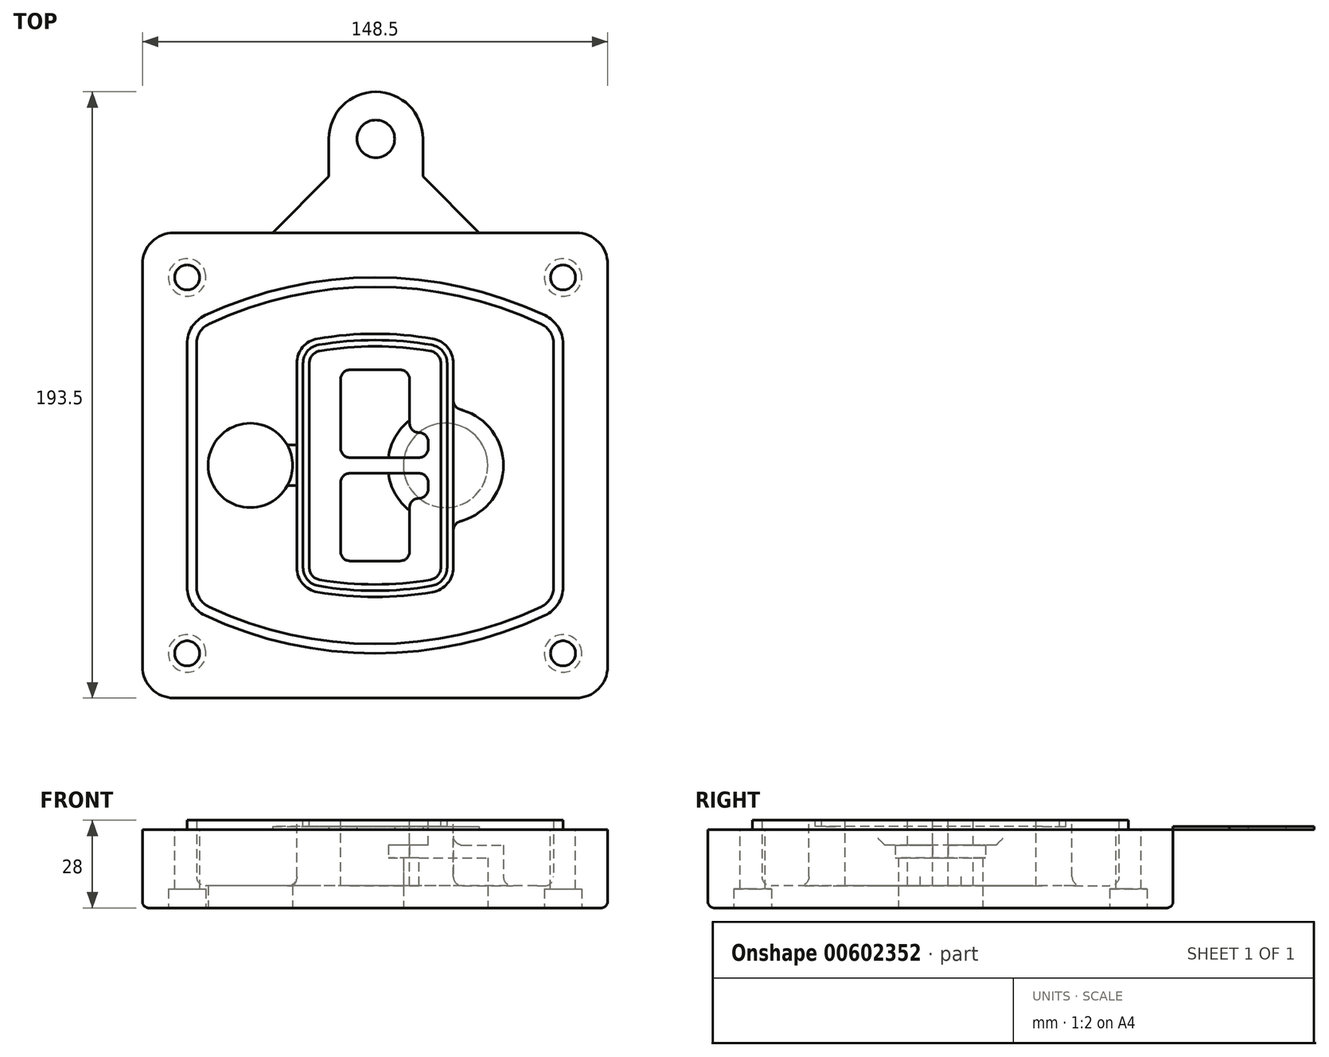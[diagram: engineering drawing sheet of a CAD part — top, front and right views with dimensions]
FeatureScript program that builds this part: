
annotation { "Feature Type Name" : "Feature", "Feature Type Description" : "" }
export const myFeature = defineFeature(function(context is Context, id is Id, definition is map)
    precondition{}
    {
        {
            var Q0;
            Q0=qCreatedBy(makeId("Top.planeOp"),FACE);
            var sketch = newSketch(context, id + "F0", { "sketchPlane" : qUnion([Q0])});
            skPoint(sketch, "E0.rect.middle", {"position": v(0, 0) * mm});
            skLineSegment(sketch, "E1.bottom", {"start": v(-64.25, -74.25) * mm, "end": v(64.25, -74.25) * mm});
            skLineSegment(sketch, "E1.top", {"start": v(-64.25, 74.25) * mm, "end": v(64.25, 74.25) * mm});
            skLineSegment(sketch, "E1.left", {"start": v(-74.25, -64.25) * mm, "end": v(-74.25, 64.25) * mm});
            skLineSegment(sketch, "E1.right", {"start": v(74.25, -64.25) * mm, "end": v(74.25, 64.25) * mm});
            skLineSegment(sketch, "E2", {"start": v(-74.25, 74.25) * mm, "end": v(74.25, -74.25) * mm, "construction": true});
            skLineSegment(sketch, "E3", {"start": v(74.25, 74.25) * mm, "end": v(-74.25, -74.25) * mm, "construction": true});
            skCircle(sketch, "E4", {"center": v(-60, 60) * mm, "radius": 4 * mm});
            skCircle(sketch, "E5", {"center": v(60, 60) * mm, "radius": 4 * mm});
            skCircle(sketch, "E6", {"center": v(60, -60) * mm, "radius": 4 * mm});
            skCircle(sketch, "E7", {"center": v(-60, -60) * mm, "radius": 4 * mm});
            skLineSegment(sketch, "E8", {"start": v(-60, 60) * mm, "end": v(60, 60) * mm, "construction": true});
            skLineSegment(sketch, "E9", {"start": v(60, 60) * mm, "end": v(60, -60) * mm, "construction": true});
            skLineSegment(sketch, "E10", {"start": v(60, -60) * mm, "end": v(-60, -60) * mm, "construction": true});
            skLineSegment(sketch, "E11", {"start": v(-60, -60) * mm, "end": v(-60, 60) * mm, "construction": true});
            skLineSegment(sketch, "E12", {"start": v(-60, 38.83) * mm, "end": v(-60, -38.83) * mm});
            skLineSegment(sketch, "E13", {"start": v(60, 38.83) * mm, "end": v(60, -38.83) * mm});
            skArc(sketch, "E14", {"start": v(54.26, 47.88) * mm, "mid": v(0, 60) * mm, "end": v(-54.26, 47.88) * mm});
            skArc(sketch, "E15", {"start": v(-54.26, -47.88) * mm, "mid": v(0, -60) * mm, "end": v(54.26, -47.88) * mm});
            skLineSegment(sketch, "E16", {"start": v(-60, 0) * mm, "end": v(60, 0) * mm, "construction": true});
            skPoint(sketch, "E17.visualSharp", {"position": v(-60, -45) * mm});
            skArc(sketch, "E17.filletArc", {"start": v(-60, -38.83) * mm, "mid": v(-58.44, -44.2) * mm, "end": v(-54.26, -47.88) * mm});
            skPoint(sketch, "E18.visualSharp", {"position": v(-60, 45) * mm});
            skArc(sketch, "E18.filletArc", {"start": v(-54.26, 47.88) * mm, "mid": v(-58.44, 44.2) * mm, "end": v(-60, 38.83) * mm});
            skPoint(sketch, "E19.visualSharp", {"position": v(60, 45) * mm});
            skArc(sketch, "E19.filletArc", {"start": v(60, 38.83) * mm, "mid": v(58.44, 44.2) * mm, "end": v(54.26, 47.88) * mm});
            skPoint(sketch, "E20.visualSharp", {"position": v(60, -45) * mm});
            skArc(sketch, "E20.filletArc", {"start": v(54.26, -47.88) * mm, "mid": v(58.44, -44.2) * mm, "end": v(60, -38.83) * mm});
            skPoint(sketch, "E21.visualSharp", {"position": v(-74.25, 74.25) * mm});
            skArc(sketch, "E21.filletArc", {"start": v(-64.25, 74.25) * mm, "mid": v(-71.32, 71.32) * mm, "end": v(-74.25, 64.25) * mm});
            skPoint(sketch, "E22.visualSharp", {"position": v(74.25, 74.25) * mm});
            skArc(sketch, "E22.filletArc", {"start": v(74.25, 64.25) * mm, "mid": v(71.32, 71.32) * mm, "end": v(64.25, 74.25) * mm});
            skPoint(sketch, "E23.visualSharp", {"position": v(74.25, -74.25) * mm});
            skArc(sketch, "E23.filletArc", {"start": v(64.25, -74.25) * mm, "mid": v(71.32, -71.32) * mm, "end": v(74.25, -64.25) * mm});
            skPoint(sketch, "E24.visualSharp", {"position": v(-74.25, -74.25) * mm});
            skArc(sketch, "E24.filletArc", {"start": v(-74.25, -64.25) * mm, "mid": v(-71.32, -71.32) * mm, "end": v(-64.25, -74.25) * mm});
            skArc(sketch, "E25.0", {"start": v(57, 38.83) * mm, "mid": v(55.9, 42.58) * mm, "end": v(52.98, 45.17) * mm});
            skLineSegment(sketch, "E25.1", {"start": v(57, 38.83) * mm, "end": v(57, -38.83) * mm});
            skArc(sketch, "E25.2", {"start": v(52.98, -45.17) * mm, "mid": v(55.9, -42.58) * mm, "end": v(57, -38.83) * mm});
            skArc(sketch, "E25.3", {"start": v(-52.98, -45.17) * mm, "mid": v(0, -57) * mm, "end": v(52.98, -45.17) * mm});
            skArc(sketch, "E25.4", {"start": v(-57, -38.83) * mm, "mid": v(-55.9, -42.58) * mm, "end": v(-52.98, -45.17) * mm});
            skArc(sketch, "E25.5", {"start": v(52.98, 45.17) * mm, "mid": v(0, 57) * mm, "end": v(-52.98, 45.17) * mm});
            skLineSegment(sketch, "E25.6", {"start": v(-57, 38.83) * mm, "end": v(-57, -38.83) * mm});
            skArc(sketch, "E25.7", {"start": v(-52.98, 45.17) * mm, "mid": v(-55.9, 42.58) * mm, "end": v(-57, 38.83) * mm});
            skArc(sketch, "E26.0", {"start": v(-55.96, 51.5) * mm, "mid": v(-61.82, 46.33) * mm, "end": v(-64, 38.83) * mm});
            skArc(sketch, "E26.1", {"start": v(55.96, 51.5) * mm, "mid": v(0, 64) * mm, "end": v(-55.96, 51.5) * mm});
            skArc(sketch, "E26.2", {"start": v(64, 38.83) * mm, "mid": v(61.82, 46.33) * mm, "end": v(55.96, 51.5) * mm});
            skLineSegment(sketch, "E26.3", {"start": v(64, 38.83) * mm, "end": v(64, -38.83) * mm});
            skArc(sketch, "E26.4", {"start": v(55.96, -51.5) * mm, "mid": v(61.82, -46.33) * mm, "end": v(64, -38.83) * mm});
            skLineSegment(sketch, "E26.5", {"start": v(-64, 38.83) * mm, "end": v(-64, -38.83) * mm});
            skArc(sketch, "E26.6", {"start": v(-55.96, -51.5) * mm, "mid": v(0, -64) * mm, "end": v(55.96, -51.5) * mm});
            skArc(sketch, "E26.7", {"start": v(-64, -38.83) * mm, "mid": v(-61.82, -46.33) * mm, "end": v(-55.96, -51.5) * mm});
            skSolve(sketch);
        }
        {
            var Q0;
            Q0=makeQuery(id+"F0.imprint","IMPRINT",FACE,{"disambiguationData":[TD([[makeQuery(id+"F0.imprint","IMPRINT",EDGE,{"derivedFrom":sQuery(id+"F0.wireOp",EDGE,"E1.bottom")}),1.0]])]});
            var Q1;
            Q1=makeQuery(id+"F0.imprint","IMPRINT",FACE,{"disambiguationData":[TD([[makeQuery(id+"F0.imprint","IMPRINT",EDGE,{"derivedFrom":sQuery(id+"F0.wireOp",EDGE,"E12")}),1.0]])]});
            var Q2;
            Q2=makeQuery(id+"F0.imprint","IMPRINT",FACE,{"disambiguationData":[TD([[makeQuery(id+"F0.imprint","IMPRINT",EDGE,{"derivedFrom":sQuery(id+"F0.wireOp",EDGE,"E25.0")}),1.0]])]});
            var Q3;
            Q3=makeQuery(id+"F0.imprint","IMPRINT",FACE,{"disambiguationData":[TD([[makeQuery(id+"F0.imprint","IMPRINT",EDGE,{"derivedFrom":sQuery(id+"F0.wireOp",EDGE,"E12")}),-1.0]])]});
            extrude(context, id + "F1", {"entities" : qUnion([Q0, Q1, Q2, Q3]), "oppositeDirection" : true, "depth" : 25 * mm});
        }
        {
            var Q0;
            Q0=makeQuery(id+"F0.imprint","IMPRINT",FACE,{"disambiguationData":[TD([[makeQuery(id+"F0.imprint","IMPRINT",EDGE,{"derivedFrom":sQuery(id+"F0.wireOp",EDGE,"E12")}),1.0]])]});
            extrude(context, id + "F2", {"entities" : qUnion([Q0]), "operationType" : NewBodyOperationType.ADD, "depth" : 3 * mm});
        }
        {
            var Q0;
            Q0=makeQuery(id+"F0.imprint","IMPRINT",FACE,{"disambiguationData":[TD([[makeQuery(id+"F0.imprint","IMPRINT",EDGE,{"derivedFrom":sQuery(id+"F0.wireOp",EDGE,"E25.0")}),1.0]])]});
            extrude(context, id + "F3", {"entities" : qUnion([Q0]), "operationType" : NewBodyOperationType.REMOVE, "oppositeDirection" : true, "depth" : 18 * mm});
        }
        {
            var Q0;
            Q0=makeQuery(id+"F2.opExtrude","CAP_FACE",FACE,{"disambiguationData":[OSD([sQuery(id+"F0.wireOp",EDGE,"E12"),sQuery(id+"F0.wireOp",EDGE,"E13"),sQuery(id+"F0.wireOp",EDGE,"E14"),sQuery(id+"F0.wireOp",EDGE,"E15"),sQuery(id+"F0.wireOp",EDGE,"E17.filletArc"),sQuery(id+"F0.wireOp",EDGE,"E18.filletArc"),sQuery(id+"F0.wireOp",EDGE,"E19.filletArc"),sQuery(id+"F0.wireOp",EDGE,"E20.filletArc"),sQuery(id+"F0.wireOp",EDGE,"E25.0"),sQuery(id+"F0.wireOp",EDGE,"E25.1"),sQuery(id+"F0.wireOp",EDGE,"E25.2"),sQuery(id+"F0.wireOp",EDGE,"E25.3"),sQuery(id+"F0.wireOp",EDGE,"E25.4"),sQuery(id+"F0.wireOp",EDGE,"E25.5"),sQuery(id+"F0.wireOp",EDGE,"E25.6"),sQuery(id+"F0.wireOp",EDGE,"E25.7")])],"isStart":false});
            var sketch = newSketch(context, id + "F4", { "sketchPlane" : qUnion([Q0])});
            skArc(sketch, "E27.0", {"start": v(-18.34, -40.45) * mm, "mid": v(0, -42) * mm, "end": v(18.34, -40.45) * mm});
            skArc(sketch, "E28.0", {"start": v(18.34, 40.45) * mm, "mid": v(0, 42) * mm, "end": v(-18.34, 40.45) * mm});
            skLineSegment(sketch, "E29", {"start": v(-25, 32.57) * mm, "end": v(-25, -32.57) * mm});
            skLineSegment(sketch, "E30", {"start": v(25, 32.57) * mm, "end": v(25, -32.57) * mm});
            skLineSegment(sketch, "E31", {"start": v(-25, 39.1) * mm, "end": v(25, 39.1) * mm, "construction": true});
            skLineSegment(sketch, "E32", {"start": v(-25, -39.1) * mm, "end": v(25, -39.1) * mm, "construction": true});
            skPoint(sketch, "E33.visualSharp", {"position": v(-25, 39.1) * mm});
            skArc(sketch, "E33.filletArc", {"start": v(-18.34, 40.45) * mm, "mid": v(-23.11, 37.73) * mm, "end": v(-25, 32.57) * mm});
            skPoint(sketch, "E34.visualSharp", {"position": v(25, 39.1) * mm});
            skArc(sketch, "E34.filletArc", {"start": v(25, 32.57) * mm, "mid": v(23.11, 37.73) * mm, "end": v(18.34, 40.45) * mm});
            skPoint(sketch, "E35.visualSharp", {"position": v(25, -39.1) * mm});
            skArc(sketch, "E35.filletArc", {"start": v(18.34, -40.45) * mm, "mid": v(23.11, -37.73) * mm, "end": v(25, -32.57) * mm});
            skPoint(sketch, "E36.visualSharp", {"position": v(-25, -39.1) * mm});
            skArc(sketch, "E36.filletArc", {"start": v(-25, -32.57) * mm, "mid": v(-23.11, -37.73) * mm, "end": v(-18.34, -40.45) * mm});
            skArc(sketch, "E37.0", {"start": v(52.98, 45.17) * mm, "mid": v(0, 57) * mm, "end": v(-52.98, 45.17) * mm});
            skArc(sketch, "E37.1", {"start": v(-52.98, 45.17) * mm, "mid": v(-55.9, 42.58) * mm, "end": v(-57, 38.83) * mm});
            skLineSegment(sketch, "E37.2", {"start": v(-57, 38.83) * mm, "end": v(-57, -38.83) * mm});
            skArc(sketch, "E37.3", {"start": v(-57, -38.83) * mm, "mid": v(-55.9, -42.58) * mm, "end": v(-52.98, -45.17) * mm});
            skArc(sketch, "E37.4", {"start": v(-52.98, -45.17) * mm, "mid": v(0, -57) * mm, "end": v(52.98, -45.17) * mm});
            skArc(sketch, "E37.5", {"start": v(52.98, -45.17) * mm, "mid": v(55.9, -42.58) * mm, "end": v(57, -38.83) * mm});
            skLineSegment(sketch, "E37.6", {"start": v(57, 38.83) * mm, "end": v(57, -38.83) * mm});
            skArc(sketch, "E37.7", {"start": v(57, 38.83) * mm, "mid": v(55.9, 42.58) * mm, "end": v(52.98, 45.17) * mm});
            skLineSegment(sketch, "E38.0", {"start": v(23, 32.57) * mm, "end": v(23, -32.57) * mm});
            skArc(sketch, "E38.1", {"start": v(18, -38.48) * mm, "mid": v(21.58, -36.44) * mm, "end": v(23, -32.57) * mm});
            skArc(sketch, "E38.2", {"start": v(-18, -38.48) * mm, "mid": v(0, -40) * mm, "end": v(18, -38.48) * mm});
            skArc(sketch, "E38.3", {"start": v(-23, -32.57) * mm, "mid": v(-21.58, -36.44) * mm, "end": v(-18, -38.48) * mm});
            skLineSegment(sketch, "E38.4", {"start": v(-23, 32.57) * mm, "end": v(-23, -32.57) * mm});
            skArc(sketch, "E38.5", {"start": v(23, 32.57) * mm, "mid": v(21.58, 36.44) * mm, "end": v(18, 38.48) * mm});
            skArc(sketch, "E38.6", {"start": v(-18, 38.48) * mm, "mid": v(-21.58, 36.44) * mm, "end": v(-23, 32.57) * mm});
            skArc(sketch, "E38.7", {"start": v(18, 38.48) * mm, "mid": v(0, 40) * mm, "end": v(-18, 38.48) * mm});
            skArc(sketch, "E39.0", {"start": v(21, 32.57) * mm, "mid": v(20.06, 35.15) * mm, "end": v(17.67, 36.5) * mm});
            skLineSegment(sketch, "E39.1", {"start": v(21, 32.57) * mm, "end": v(21, -32.57) * mm});
            skArc(sketch, "E39.2", {"start": v(17.67, -36.5) * mm, "mid": v(20.06, -35.15) * mm, "end": v(21, -32.57) * mm});
            skArc(sketch, "E39.3", {"start": v(-17.67, -36.5) * mm, "mid": v(0, -38) * mm, "end": v(17.67, -36.5) * mm});
            skArc(sketch, "E39.4", {"start": v(-21, -32.57) * mm, "mid": v(-20.06, -35.15) * mm, "end": v(-17.67, -36.5) * mm});
            skArc(sketch, "E39.5", {"start": v(17.67, 36.5) * mm, "mid": v(0, 38) * mm, "end": v(-17.67, 36.5) * mm});
            skLineSegment(sketch, "E39.6", {"start": v(-21, 32.57) * mm, "end": v(-21, -32.57) * mm});
            skArc(sketch, "E39.7", {"start": v(-17.67, 36.5) * mm, "mid": v(-20.06, 35.15) * mm, "end": v(-21, 32.57) * mm});
            skLineSegment(sketch, "E40", {"start": v(-25, 0) * mm, "end": v(25, 0) * mm, "construction": true});
            skLineSegment(sketch, "E41", {"start": v(-11, 5.5) * mm, "end": v(-11, 27.5) * mm});
            skLineSegment(sketch, "E42", {"start": v(-8, 30.5) * mm, "end": v(8, 30.5) * mm});
            skLineSegment(sketch, "E43", {"start": v(11, 27.5) * mm, "end": v(11, 13.5) * mm});
            skLineSegment(sketch, "E44", {"start": v(14, 10.5) * mm, "end": v(14, 10.5) * mm});
            skLineSegment(sketch, "E45", {"start": v(17, 7.5) * mm, "end": v(17, 5.5) * mm});
            skLineSegment(sketch, "E46", {"start": v(14, 2.5) * mm, "end": v(-8, 2.5) * mm});
            skPoint(sketch, "E47.visualSharp", {"position": v(-11, 30.5) * mm});
            skArc(sketch, "E47.filletArc", {"start": v(-8, 30.5) * mm, "mid": v(-10.12, 29.62) * mm, "end": v(-11, 27.5) * mm});
            skPoint(sketch, "E48.visualSharp", {"position": v(11, 30.5) * mm});
            skArc(sketch, "E48.filletArc", {"start": v(11, 27.5) * mm, "mid": v(10.12, 29.62) * mm, "end": v(8, 30.5) * mm});
            skPoint(sketch, "E49.visualSharp", {"position": v(11, 10.5) * mm});
            skArc(sketch, "E49.filletArc", {"start": v(11, 13.5) * mm, "mid": v(11.88, 11.38) * mm, "end": v(14, 10.5) * mm});
            skPoint(sketch, "E50.visualSharp", {"position": v(17, 10.5) * mm});
            skArc(sketch, "E50.filletArc", {"start": v(17, 7.5) * mm, "mid": v(16.12, 9.62) * mm, "end": v(14, 10.5) * mm});
            skPoint(sketch, "E51.visualSharp", {"position": v(17, 2.5) * mm});
            skArc(sketch, "E51.filletArc", {"start": v(14, 2.5) * mm, "mid": v(16.12, 3.38) * mm, "end": v(17, 5.5) * mm});
            skPoint(sketch, "E52.visualSharp", {"position": v(-11, 2.5) * mm});
            skArc(sketch, "E52.filletArc", {"start": v(-11, 5.5) * mm, "mid": v(-10.12, 3.38) * mm, "end": v(-8, 2.5) * mm});
            skLineSegment(sketch, "E53.0.MirrorCS", {"start": v(14, -2.5) * mm, "end": v(-8, -2.5) * mm});
            skArc(sketch, "E54.0.MirrorCS", {"start": v(-11, -5.5) * mm, "mid": v(-10.12, -3.38) * mm, "end": v(-8, -2.5) * mm});
            skLineSegment(sketch, "E55.0.MirrorCS", {"start": v(-11, -5.5) * mm, "end": v(-11, -27.5) * mm});
            skArc(sketch, "E56.0.MirrorCS", {"start": v(-8, -30.5) * mm, "mid": v(-10.12, -29.62) * mm, "end": v(-11, -27.5) * mm});
            skLineSegment(sketch, "E57.0.MirrorCS", {"start": v(-8, -30.5) * mm, "end": v(8, -30.5) * mm});
            skArc(sketch, "E58.0.MirrorCS", {"start": v(11, -27.5) * mm, "mid": v(10.12, -29.62) * mm, "end": v(8, -30.5) * mm});
            skLineSegment(sketch, "E59.0.MirrorCS", {"start": v(11, -27.5) * mm, "end": v(11, -13.5) * mm});
            skArc(sketch, "E60.0.MirrorCS", {"start": v(11, -13.5) * mm, "mid": v(11.88, -11.38) * mm, "end": v(14, -10.5) * mm});
            skArc(sketch, "E61.0.MirrorCS", {"start": v(17, -7.5) * mm, "mid": v(16.12, -9.62) * mm, "end": v(14, -10.5) * mm});
            skLineSegment(sketch, "E62.0.MirrorCS", {"start": v(17, -7.5) * mm, "end": v(17, -5.5) * mm});
            skArc(sketch, "E63.0.MirrorCS", {"start": v(14, -2.5) * mm, "mid": v(16.12, -3.38) * mm, "end": v(17, -5.5) * mm});
            skSolve(sketch);
        }
        {
            var Q0;
            Q0=makeQuery(id+"F4.imprint","IMPRINT",FACE,{"disambiguationData":[TD([[makeQuery(id+"F4.imprint","IMPRINT",EDGE,{"derivedFrom":sQuery(id+"F4.wireOp",EDGE,"E27.0")}),1.0]])]});
            var Q1;
            Q1=makeQuery(id+"F4.imprint","IMPRINT",FACE,{"disambiguationData":[TD([[makeQuery(id+"F4.imprint","IMPRINT",EDGE,{"derivedFrom":sQuery(id+"F4.wireOp",EDGE,"E38.0")}),-1.0]])]});
            var Q2;
            Q2=makeQuery(id+"F4.imprint","IMPRINT",FACE,{"disambiguationData":[TD([[makeQuery(id+"F4.imprint","IMPRINT",EDGE,{"derivedFrom":sQuery(id+"F4.wireOp",EDGE,"E39.0")}),1.0]])]});
            extrude(context, id + "F5", {"entities" : qUnion([Q0, Q1, Q2]), "operationType" : NewBodyOperationType.ADD, "endBound" : BoundingType.UP_TO_NEXT, "oppositeDirection" : true, "depth" : 25 * mm});
        }
        {
            var Q0;
            Q0=makeQuery(id+"F4.imprint","IMPRINT",FACE,{"disambiguationData":[TD([[makeQuery(id+"F4.imprint","IMPRINT",EDGE,{"derivedFrom":sQuery(id+"F4.wireOp",EDGE,"E38.0")}),-1.0]])]});
            extrude(context, id + "F6", {"entities" : qUnion([Q0]), "operationType" : NewBodyOperationType.REMOVE, "oppositeDirection" : true, "depth" : 2 * mm});
        }
        {
            var Q0;
            Q0=makeQuery(id+"F1.opExtrude","CAP_FACE",FACE,{"disambiguationData":[OSD([sQuery(id+"F0.wireOp",EDGE,"E1.bottom"),sQuery(id+"F0.wireOp",EDGE,"E1.top"),sQuery(id+"F0.wireOp",EDGE,"E1.left"),sQuery(id+"F0.wireOp",EDGE,"E1.right"),sQuery(id+"F0.wireOp",EDGE,"E4"),sQuery(id+"F0.wireOp",EDGE,"E5"),sQuery(id+"F0.wireOp",EDGE,"E6"),sQuery(id+"F0.wireOp",EDGE,"E7"),sQuery(id+"F0.wireOp",EDGE,"E21.filletArc"),sQuery(id+"F0.wireOp",EDGE,"E22.filletArc"),sQuery(id+"F0.wireOp",EDGE,"E23.filletArc"),sQuery(id+"F0.wireOp",EDGE,"E24.filletArc")])],"isStart":false});
            var sketch = newSketch(context, id + "F7", { "sketchPlane" : qUnion([Q0])});
            skCircle(sketch, "E64", {"center": v(22.5, 0) * mm, "radius": 13.47 * mm});
            skCircle(sketch, "E65", {"center": v(-39.81, 0) * mm, "radius": 13.47 * mm});
            skLineSegment(sketch, "E66", {"start": v(74.25, 0) * mm, "end": v(-74.25, 0) * mm});
            skCircle(sketch, "E67", {"center": v(22.5, 0) * mm, "radius": 18.47 * mm});
            skCircle(sketch, "E68", {"center": v(60, -60) * mm, "radius": 6 * mm});
            skCircle(sketch, "E69", {"center": v(-60, -60) * mm, "radius": 6 * mm});
            skCircle(sketch, "E70", {"center": v(-60, 60) * mm, "radius": 6 * mm});
            skCircle(sketch, "E71", {"center": v(60, 60) * mm, "radius": 6 * mm});
            skSolve(sketch);
        }
        {
            var Q0;
            {var subQ1=sQuery(id+"F7.wireOp",EDGE,"E66");var subQ4=sQuery(id+"F7.wireOp",EDGE,"E64");var subQ6=makeQuery(id+"F7.imprint","INTERSECT",VERTEX,{"disambiguationData":[OD(0.0)],"derivedFrom":[subQ4,subQ1]});Q0=makeQuery(id+"F7.imprint","IMPRINT",FACE,{"disambiguationData":[TD([[makeQuery(id+"F7.imprint","IMPRINT",EDGE,{"disambiguationData":[TD([[subQ6,-1.0]])],"derivedFrom":subQ4}),-1.0]])]});}
            var Q1;
            {var subQ0=sQuery(id+"F7.wireOp",EDGE,"E66");var subQ1=sQuery(id+"F7.wireOp",EDGE,"E64");var subQ3=makeQuery(id+"F7.imprint","INTERSECT",VERTEX,{"disambiguationData":[OD(0.0)],"derivedFrom":[subQ1,subQ0]});Q1=makeQuery(id+"F7.imprint","IMPRINT",FACE,{"disambiguationData":[TD([[makeQuery(id+"F7.imprint","IMPRINT",EDGE,{"disambiguationData":[TD([[subQ3,-1.0]])],"derivedFrom":subQ1}),1.0]])]});}
            var Q2;
            {var subQ0=sQuery(id+"F7.wireOp",EDGE,"E66");var subQ1=sQuery(id+"F7.wireOp",EDGE,"E64");var subQ3=makeQuery(id+"F7.imprint","INTERSECT",VERTEX,{"disambiguationData":[OD(0.0)],"derivedFrom":[subQ1,subQ0]});Q2=makeQuery(id+"F7.imprint","IMPRINT",FACE,{"disambiguationData":[TD([[makeQuery(id+"F7.imprint","IMPRINT",EDGE,{"disambiguationData":[TD([[subQ3,1.0]])],"derivedFrom":subQ1}),1.0]])]});}
            var Q3;
            {var subQ1=sQuery(id+"F7.wireOp",EDGE,"E66");var subQ4=sQuery(id+"F7.wireOp",EDGE,"E64");var subQ6=makeQuery(id+"F7.imprint","INTERSECT",VERTEX,{"disambiguationData":[OD(0.0)],"derivedFrom":[subQ4,subQ1]});Q3=makeQuery(id+"F7.imprint","IMPRINT",FACE,{"disambiguationData":[TD([[makeQuery(id+"F7.imprint","IMPRINT",EDGE,{"disambiguationData":[TD([[subQ6,1.0]])],"derivedFrom":subQ4}),-1.0]])]});}
            extrude(context, id + "F8", {"entities" : qUnion([Q0, Q1, Q2, Q3]), "operationType" : NewBodyOperationType.ADD, "oppositeDirection" : true, "depth" : 20 * mm});
        }
        {
            var Q0;
            {var subQ0=sQuery(id+"F7.wireOp",EDGE,"E66");var subQ1=sQuery(id+"F7.wireOp",EDGE,"E64");var subQ3=makeQuery(id+"F7.imprint","INTERSECT",VERTEX,{"disambiguationData":[OD(0.0)],"derivedFrom":[subQ1,subQ0]});Q0=makeQuery(id+"F7.imprint","IMPRINT",FACE,{"disambiguationData":[TD([[makeQuery(id+"F7.imprint","IMPRINT",EDGE,{"disambiguationData":[TD([[subQ3,-1.0]])],"derivedFrom":subQ1}),1.0]])]});}
            var Q1;
            {var subQ0=sQuery(id+"F7.wireOp",EDGE,"E66");var subQ1=sQuery(id+"F7.wireOp",EDGE,"E64");var subQ3=makeQuery(id+"F7.imprint","INTERSECT",VERTEX,{"disambiguationData":[OD(0.0)],"derivedFrom":[subQ1,subQ0]});Q1=makeQuery(id+"F7.imprint","IMPRINT",FACE,{"disambiguationData":[TD([[makeQuery(id+"F7.imprint","IMPRINT",EDGE,{"disambiguationData":[TD([[subQ3,1.0]])],"derivedFrom":subQ1}),1.0]])]});}
            extrude(context, id + "F9", {"entities" : qUnion([Q0, Q1]), "operationType" : NewBodyOperationType.REMOVE, "oppositeDirection" : true, "depth" : 16 * mm});
        }
        {
            var Q0;
            {var subQ0=sQuery(id+"F7.wireOp",EDGE,"E66");var subQ1=sQuery(id+"F7.wireOp",EDGE,"E65");var subQ3=makeQuery(id+"F7.imprint","INTERSECT",VERTEX,{"disambiguationData":[OD(0.0)],"derivedFrom":[subQ1,subQ0]});Q0=makeQuery(id+"F7.imprint","IMPRINT",FACE,{"disambiguationData":[TD([[makeQuery(id+"F7.imprint","IMPRINT",EDGE,{"disambiguationData":[TD([[subQ3,-1.0]])],"derivedFrom":subQ1}),1.0]])]});}
            var Q1;
            {var subQ0=sQuery(id+"F7.wireOp",EDGE,"E66");var subQ1=sQuery(id+"F7.wireOp",EDGE,"E65");var subQ3=makeQuery(id+"F7.imprint","INTERSECT",VERTEX,{"disambiguationData":[OD(0.0)],"derivedFrom":[subQ1,subQ0]});Q1=makeQuery(id+"F7.imprint","IMPRINT",FACE,{"disambiguationData":[TD([[makeQuery(id+"F7.imprint","IMPRINT",EDGE,{"disambiguationData":[TD([[subQ3,1.0]])],"derivedFrom":subQ1}),1.0]])]});}
            extrude(context, id + "F10", {"entities" : qUnion([Q0, Q1]), "operationType" : NewBodyOperationType.REMOVE, "oppositeDirection" : true, "depth" : 25 * mm});
        }
        {
            var Q0;
            Q0=makeQuery(id+"F7.imprint","IMPRINT",FACE,{"disambiguationData":[TD([[makeQuery(id+"F7.imprint","IMPRINT",EDGE,{"derivedFrom":sQuery(id+"F7.wireOp",EDGE,"E68")}),1.0]])]});
            var Q1;
            Q1=makeQuery(id+"F7.imprint","IMPRINT",FACE,{"disambiguationData":[TD([[makeQuery(id+"F7.imprint","IMPRINT",EDGE,{"derivedFrom":makeQuery(id+"F1.opExtrude","CAP_EDGE",EDGE,{"disambiguationData":[OSD([sQuery(id+"F0.wireOp",EDGE,"E5")])],"isStart":false})}),-1.0]])]});
            var Q2;
            Q2=makeQuery(id+"F7.imprint","IMPRINT",FACE,{"disambiguationData":[TD([[makeQuery(id+"F7.imprint","IMPRINT",EDGE,{"derivedFrom":sQuery(id+"F7.wireOp",EDGE,"E69")}),1.0]])]});
            var Q3;
            Q3=makeQuery(id+"F7.imprint","IMPRINT",FACE,{"disambiguationData":[TD([[makeQuery(id+"F7.imprint","IMPRINT",EDGE,{"derivedFrom":makeQuery(id+"F1.opExtrude","CAP_EDGE",EDGE,{"disambiguationData":[OSD([sQuery(id+"F0.wireOp",EDGE,"E4")])],"isStart":false})}),-1.0]])]});
            var Q4;
            Q4=makeQuery(id+"F7.imprint","IMPRINT",FACE,{"disambiguationData":[TD([[makeQuery(id+"F7.imprint","IMPRINT",EDGE,{"derivedFrom":sQuery(id+"F7.wireOp",EDGE,"E70")}),1.0]])]});
            var Q5;
            Q5=makeQuery(id+"F7.imprint","IMPRINT",FACE,{"disambiguationData":[TD([[makeQuery(id+"F7.imprint","IMPRINT",EDGE,{"derivedFrom":makeQuery(id+"F1.opExtrude","CAP_EDGE",EDGE,{"disambiguationData":[OSD([sQuery(id+"F0.wireOp",EDGE,"E7")])],"isStart":false})}),-1.0]])]});
            var Q6;
            Q6=makeQuery(id+"F7.imprint","IMPRINT",FACE,{"disambiguationData":[TD([[makeQuery(id+"F7.imprint","IMPRINT",EDGE,{"derivedFrom":sQuery(id+"F7.wireOp",EDGE,"E71")}),1.0]])]});
            var Q7;
            Q7=makeQuery(id+"F7.imprint","IMPRINT",FACE,{"disambiguationData":[TD([[makeQuery(id+"F7.imprint","IMPRINT",EDGE,{"derivedFrom":makeQuery(id+"F1.opExtrude","CAP_EDGE",EDGE,{"disambiguationData":[OSD([sQuery(id+"F0.wireOp",EDGE,"E6")])],"isStart":false})}),-1.0]])]});
            extrude(context, id + "F11", {"entities" : qUnion([Q0, Q1, Q2, Q3, Q4, Q5, Q6, Q7]), "operationType" : NewBodyOperationType.REMOVE, "oppositeDirection" : true, "depth" : 6 * mm});
        }
        {
            var Q0;
            Q0=makeQuery(id+"F9.boolean.opBoolean","COPY",FACE,{"derivedFrom":makeQuery(id+"F9.opExtrude","CAP_FACE",FACE,{"disambiguationData":[OSD([sQuery(id+"F7.wireOp",EDGE,"E64")])],"isStart":false})});
            var sketch = newSketch(context, id + "F12", { "sketchPlane" : qUnion([Q0])});
            skArc(sketch, "E72.0", {"start": v(11, 14.45) * mm, "mid": v(6.45, 9.13) * mm, "end": v(4.2, 2.5) * mm});
            skArc(sketch, "E72.1", {"start": v(4.2, -2.5) * mm, "mid": v(6.45, -9.13) * mm, "end": v(11, -14.45) * mm});
            skLineSegment(sketch, "E73", {"start": v(4.2, -2.5) * mm, "end": v(14, -2.5) * mm});
            skLineSegment(sketch, "E74.0", {"start": v(14, 2.5) * mm, "end": v(4.2, 2.5) * mm});
            skArc(sketch, "E74.1", {"start": v(14, 2.5) * mm, "mid": v(16.12, 3.38) * mm, "end": v(17, 5.5) * mm});
            skLineSegment(sketch, "E74.2", {"start": v(17, 7.5) * mm, "end": v(17, 5.5) * mm});
            skArc(sketch, "E74.3", {"start": v(17, 7.5) * mm, "mid": v(16.12, 9.62) * mm, "end": v(14, 10.5) * mm});
            skArc(sketch, "E74.4", {"start": v(11, 13.5) * mm, "mid": v(11.88, 11.38) * mm, "end": v(14, 10.5) * mm});
            skLineSegment(sketch, "E74.5", {"start": v(11, 14.45) * mm, "end": v(11, 13.5) * mm});
            skLineSegment(sketch, "E74.7", {"start": v(14, -2.5) * mm, "end": v(4.2, -2.5) * mm});
            skArc(sketch, "E74.8", {"start": v(14, -2.5) * mm, "mid": v(16.12, -3.38) * mm, "end": v(17, -5.5) * mm});
            skLineSegment(sketch, "E74.9", {"start": v(17, -7.5) * mm, "end": v(17, -5.5) * mm});
            skArc(sketch, "E74.10", {"start": v(17, -7.5) * mm, "mid": v(16.12, -9.62) * mm, "end": v(14, -10.5) * mm});
            skArc(sketch, "E74.11", {"start": v(11, -13.5) * mm, "mid": v(11.88, -11.38) * mm, "end": v(14, -10.5) * mm});
            skLineSegment(sketch, "E74.12", {"start": v(11, -14.45) * mm, "end": v(11, -13.5) * mm});
            skPoint(sketch, "E75.orphan", {"position": v(11, -27.5) * mm});
            skPoint(sketch, "E76.orphan", {"position": v(-8, -2.5) * mm});
            skPoint(sketch, "E77.orphan", {"position": v(-8, 2.5) * mm});
            skPoint(sketch, "E78.orphan", {"position": v(11, 27.5) * mm});
            skSolve(sketch);
        }
        {
            var Q0;
            {var subQ7=sQuery(id+"F12.wireOp",EDGE,"E72.0");var subQ14=sQuery(id+"F12.wireOp",EDGE,"E72.1");var subQ16=sQuery(id+"F12.wireOp",EDGE,"E74.1");var subQ18=sQuery(id+"F12.wireOp",EDGE,"E74.8");Q0=qUnion([makeQuery(id+"F12.imprint","IMPRINT",FACE,{"disambiguationData":[TD([[makeQuery(id+"F12.imprint","IMPRINT",EDGE,{"derivedFrom":subQ7}),1.0]])]}),makeQuery(id+"F12.imprint","IMPRINT",FACE,{"disambiguationData":[TD([[makeQuery(id+"F12.imprint","IMPRINT",EDGE,{"derivedFrom":subQ14}),1.0]])]}),makeQuery(id+"F12.imprint","IMPRINT",FACE,{"disambiguationData":[TD([[makeQuery(id+"F12.imprint","IMPRINT",EDGE,{"derivedFrom":subQ16}),1.0]])]}),makeQuery(id+"F12.imprint","IMPRINT",FACE,{"disambiguationData":[TD([[makeQuery(id+"F12.imprint","IMPRINT",EDGE,{"derivedFrom":subQ18}),-1.0]])]})]);}
            var Q1;
            Q1=makeQuery(id+"F5.boolean.opBoolean","SPLIT",FACE,{"disambiguationData":[TD([makeQuery(id+"F5.opExtrude","SWEPT_FACE",FACE,{"disambiguationData":[OSD([sQuery(id+"F4.wireOp",EDGE,"E41")])]})])],"derivedFrom":makeQuery(id+"F3.boolean.opBoolean","COPY",FACE,{"derivedFrom":makeQuery(id+"F3.opExtrude","CAP_FACE",FACE,{"disambiguationData":[OSD([sQuery(id+"F0.wireOp",EDGE,"E25.0"),sQuery(id+"F0.wireOp",EDGE,"E25.1"),sQuery(id+"F0.wireOp",EDGE,"E25.2"),sQuery(id+"F0.wireOp",EDGE,"E25.3"),sQuery(id+"F0.wireOp",EDGE,"E25.4"),sQuery(id+"F0.wireOp",EDGE,"E25.5"),sQuery(id+"F0.wireOp",EDGE,"E25.6"),sQuery(id+"F0.wireOp",EDGE,"E25.7")])],"isStart":false})})});
            extrude(context, id + "F13", {"entities" : qUnion([Q0]), "operationType" : NewBodyOperationType.REMOVE, "endBound" : BoundingType.UP_TO_SURFACE, "endBoundEntityFace" : qUnion([Q1]), "depth" : 25 * mm});
        }
        {
            var Q0;
            Q0=makeQuery(id+"F3.boolean.opBoolean","COPY",EDGE,{"derivedFrom":makeQuery(id+"F3.opExtrude","CAP_EDGE",EDGE,{"disambiguationData":[OSD([sQuery(id+"F0.wireOp",EDGE,"E25.6")])],"isStart":false})});
            var Q1;
            Q1=makeQuery(id+"F8.boolean.opBoolean","INTERSECT",EDGE,{"derivedFrom":[makeQuery(id+"F5.opExtrude","SWEPT_FACE",FACE,{"disambiguationData":[OSD([sQuery(id+"F4.wireOp",EDGE,"E30")])]}),makeQuery(id+"F8.opExtrude","CAP_FACE",FACE,{"disambiguationData":[OSD([sQuery(id+"F7.wireOp",EDGE,"E67")])],"isStart":false})]});
            var Q2;
            Q2=makeQuery(id+"F8.boolean.opBoolean","INTERSECT",EDGE,{"disambiguationData":[OD(1.0)],"derivedFrom":[makeQuery(id+"F5.opExtrude","SWEPT_FACE",FACE,{"disambiguationData":[OSD([sQuery(id+"F4.wireOp",EDGE,"E30")])]}),makeQuery(id+"F8.opExtrude","SWEPT_FACE",FACE,{"disambiguationData":[OSD([sQuery(id+"F7.wireOp",EDGE,"E67")])]})]});
            var Q3;
            {var subQ0=sQuery(id+"F4.wireOp",EDGE,"E30");Q3=makeQuery(id+"F8.boolean.opBoolean","SPLIT",EDGE,{"disambiguationData":[TD([makeQuery(id+"F5.opExtrude","SWEPT_FACE",FACE,{"disambiguationData":[OSD([sQuery(id+"F4.wireOp",EDGE,"E35.filletArc")])]})])],"derivedFrom":makeQuery(id+"F5.opExtrude","CAP_EDGE",EDGE,{"disambiguationData":[OSD([subQ0])],"isStart":false})});}
            var Q4;
            {var subQ0=sQuery(id+"F0.wireOp",EDGE,"E25.7");var subQ1=sQuery(id+"F0.wireOp",EDGE,"E25.1");var subQ2=sQuery(id+"F0.wireOp",EDGE,"E25.6");var subQ3=sQuery(id+"F0.wireOp",EDGE,"E25.5");var subQ4=sQuery(id+"F0.wireOp",EDGE,"E25.4");var subQ5=sQuery(id+"F0.wireOp",EDGE,"E25.0");var subQ6=sQuery(id+"F0.wireOp",EDGE,"E25.2");var subQ7=sQuery(id+"F0.wireOp",EDGE,"E25.3");Q4=makeQuery(id+"F8.boolean.opBoolean","INTERSECT",EDGE,{"derivedFrom":[makeQuery(id+"F5.boolean.opBoolean","SPLIT",FACE,{"disambiguationData":[TD([makeQuery(id+"F2.opExtrude","SWEPT_FACE",FACE,{"disambiguationData":[OSD([subQ5])]})])],"derivedFrom":makeQuery(id+"F3.boolean.opBoolean","COPY",FACE,{"derivedFrom":makeQuery(id+"F3.opExtrude","CAP_FACE",FACE,{"disambiguationData":[OSD([subQ5,subQ1,subQ6,subQ7,subQ4,subQ3,subQ2,subQ0])],"isStart":false})})}),makeQuery(id+"F8.opExtrude","SWEPT_FACE",FACE,{"disambiguationData":[OSD([sQuery(id+"F7.wireOp",EDGE,"E67")])]})]});}
            var Q5;
            Q5=makeQuery(id+"F8.boolean.opBoolean","INTERSECT",EDGE,{"disambiguationData":[OD(0.0)],"derivedFrom":[makeQuery(id+"F5.opExtrude","SWEPT_FACE",FACE,{"disambiguationData":[OSD([sQuery(id+"F4.wireOp",EDGE,"E30")])]}),makeQuery(id+"F8.opExtrude","SWEPT_FACE",FACE,{"disambiguationData":[OSD([sQuery(id+"F7.wireOp",EDGE,"E67")])]})]});
            fillet(context, id + "F14", {"entities" : qUnion([Q0, Q1, Q2, Q3, Q4, Q5]), "radius" : 3 * mm, "tangentPropagation" : true, "allowEdgeOverflow" : false});
        }
        {
            var Q0;
            Q0=makeQuery(id+"F1.opExtrude","CAP_EDGE",EDGE,{"disambiguationData":[OSD([sQuery(id+"F0.wireOp",EDGE,"E1.bottom")])],"isStart":false});
            fillet(context, id + "F15", {"entities" : qUnion([Q0]), "radius" : 2 * mm, "tangentPropagation" : true, "allowEdgeOverflow" : false});
        }
        {
            var Q0;
            {var subQ0=sQuery(id+"F0.wireOp",EDGE,"E21.filletArc");var subQ1=sQuery(id+"F0.wireOp",EDGE,"E7");var subQ2=sQuery(id+"F0.wireOp",EDGE,"E6");var subQ3=sQuery(id+"F0.wireOp",EDGE,"E5");var subQ4=sQuery(id+"F0.wireOp",EDGE,"E4");var subQ5=sQuery(id+"F0.wireOp",EDGE,"E22.filletArc");var subQ6=sQuery(id+"F0.wireOp",EDGE,"E1.bottom");var subQ7=sQuery(id+"F0.wireOp",EDGE,"E1.right");var subQ8=sQuery(id+"F0.wireOp",EDGE,"E1.top");var subQ9=sQuery(id+"F0.wireOp",EDGE,"E1.left");var subQ10=sQuery(id+"F0.wireOp",EDGE,"E23.filletArc");var subQ11=sQuery(id+"F0.wireOp",EDGE,"E24.filletArc");Q0=makeQuery(id+"F2.boolean.opBoolean","SPLIT",FACE,{"disambiguationData":[TD([makeQuery(id+"F1.opExtrude","SWEPT_FACE",FACE,{"disambiguationData":[OSD([subQ6])]})])],"derivedFrom":makeQuery(id+"F1.opExtrude","CAP_FACE",FACE,{"disambiguationData":[OSD([subQ6,subQ8,subQ9,subQ7,subQ4,subQ3,subQ2,subQ1,subQ0,subQ5,subQ10,subQ11])],"isStart":true})});}
            var sketch = newSketch(context, id + "F16", { "sketchPlane" : qUnion([Q0])});
            skSolve(sketch);
        }
        {
            var Q0;
            Q0=makeQuery(id+"F16.imprint","IMPRINT",FACE,{"disambiguationData":[TD([[makeQuery(id+"F16.imprint","IMPRINT",EDGE,{"derivedFrom":makeQuery(id+"F1.opExtrude","CAP_EDGE",EDGE,{"disambiguationData":[OSD([sQuery(id+"F0.wireOp",EDGE,"E1.bottom")])],"isStart":true})}),1.0]])]});
            var sketch = newSketch(context, id + "F17", { "sketchPlane" : qUnion([Q0])});
            skLineSegment(sketch, "E79", {"start": v(0, 43.7) * mm, "end": v(0, 63.28) * mm, "construction": true});
            skLineSegment(sketch, "E80", {"start": v(0, 63.28) * mm, "end": v(0.25, 104.25) * mm, "construction": true});
            skCircle(sketch, "E81", {"center": v(0.25, 104.25) * mm, "radius": 6 * mm});
            skLineSegment(sketch, "E82", {"start": v(0, 43.7) * mm, "end": v(0, 42.93) * mm});
            skLineSegment(sketch, "E83", {"start": v(-14.75, 92.25) * mm, "end": v(-14.75, 104.25) * mm});
            skLineSegment(sketch, "E84", {"start": v(15.25, 92.25) * mm, "end": v(15.25, 104.25) * mm});
            skArc(sketch, "E85", {"start": v(15.25, 104.25) * mm, "mid": v(0.25, 119.25) * mm, "end": v(-14.75, 104.25) * mm});
            skLineSegment(sketch, "E86", {"start": v(-14.75, 92.25) * mm, "end": v(-32.75, 74.25) * mm});
            skLineSegment(sketch, "E87", {"start": v(15.25, 92.25) * mm, "end": v(33.25, 74.25) * mm});
            skLineSegment(sketch, "E88", {"start": v(-81, 0) * mm, "end": v(83.09, 0) * mm, "construction": true});
            skArc(sketch, "E89.MirrorCS", {"start": v(15.25, -104.25) * mm, "mid": v(0.25, -119.25) * mm, "end": v(-14.75, -104.25) * mm});
            skLineSegment(sketch, "E90.MirrorCS", {"start": v(-14.75, -92.25) * mm, "end": v(-14.75, -104.25) * mm});
            skLineSegment(sketch, "E91.MirrorCS", {"start": v(15.25, -92.25) * mm, "end": v(33.25, -74.25) * mm});
            skLineSegment(sketch, "E92.MirrorCS", {"start": v(-14.75, -92.25) * mm, "end": v(-32.75, -74.25) * mm});
            skLineSegment(sketch, "E93.MirrorCS", {"start": v(15.25, -92.25) * mm, "end": v(15.25, -104.25) * mm});
            skCircle(sketch, "E94.MirrorC", {"center": v(0.25, -104.25) * mm, "radius": 6 * mm});
            skLineSegment(sketch, "E95", {"start": v(0, 42.93) * mm, "end": v(0.25, -104.25) * mm, "construction": true});
            skSolve(sketch);
        }
        {
            var Q0;
            Q0=makeQuery(id+"F17.imprint","IMPRINT",FACE,{"disambiguationData":[TD([[makeQuery(id+"F17.imprint","IMPRINT",EDGE,{"derivedFrom":sQuery(id+"F17.wireOp",EDGE,"E81")}),-1.0]])]});
            var Q1;
            Q1=makeQuery(id+"F17.imprint","IMPRINT",FACE,{"disambiguationData":[TD([[makeQuery(id+"F17.imprint","IMPRINT",EDGE,{"derivedFrom":sQuery(id+"F17.wireOp",EDGE,"E89.MirrorCS")}),-1.0]])]});
            extrude(context, id + "F18", {"entities" : qUnion([Q0, Q1]), "depth" : 1 * mm, "offsetDistance" : 25 * mm});
        }
    });
